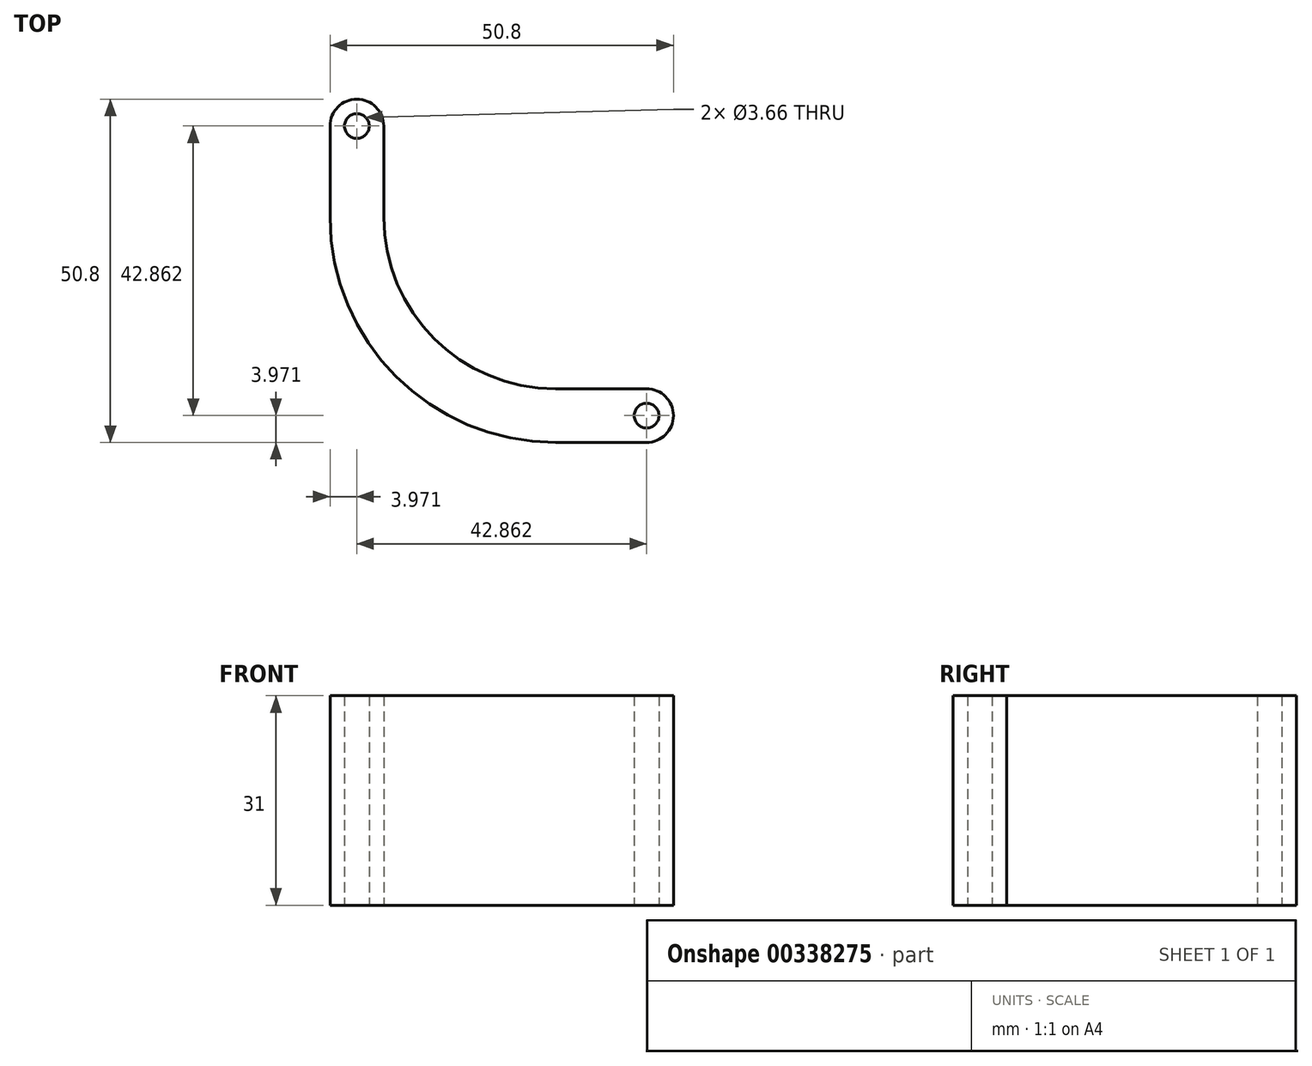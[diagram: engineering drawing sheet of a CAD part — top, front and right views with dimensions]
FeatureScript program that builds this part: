
annotation { "Feature Type Name" : "Feature", "Feature Type Description" : "" }
export const myFeature = defineFeature(function(context is Context, id is Id, definition is map)
    precondition{}
    {
        {
            var Q0;
            Q0=qCreatedBy(makeId("Top.planeOp"),FACE);
            var sketch = newSketch(context, id + "F0", { "sketchPlane" : qUnion([Q0])});
            skArc(sketch, "E0", {"start": v(-25.4, 0) * mm, "mid": v(-17.96, -17.96) * mm, "end": v(0, -25.4) * mm});
            skLineSegment(sketch, "E1.top", {"start": v(-25.4, 13.5) * mm, "end": v(-33.34, 13.5) * mm, "construction": true});
            skLineSegment(sketch, "E1.left", {"start": v(-25.4, 0) * mm, "end": v(-25.4, 13.5) * mm});
            skLineSegment(sketch, "E1.right", {"start": v(-33.34, 0) * mm, "end": v(-33.34, 13.5) * mm});
            skLineSegment(sketch, "E2.bottom", {"start": v(0, -25.4) * mm, "end": v(13.5, -25.4) * mm});
            skLineSegment(sketch, "E2.top", {"start": v(0, -33.34) * mm, "end": v(13.5, -33.34) * mm});
            skLineSegment(sketch, "E2.right", {"start": v(13.5, -25.4) * mm, "end": v(13.5, -33.34) * mm, "construction": true});
            skArc(sketch, "E3", {"start": v(-33.34, 0) * mm, "mid": v(-23.57, -23.57) * mm, "end": v(0, -33.34) * mm});
            skLineSegment(sketch, "E4", {"start": v(-33.34, 0) * mm, "end": v(-33.34, -33.34) * mm, "construction": true});
            skLineSegment(sketch, "E5", {"start": v(-33.34, -33.34) * mm, "end": v(0, -33.34) * mm, "construction": true});
            skArc(sketch, "E6", {"start": v(13.5, -33.34) * mm, "mid": v(17.46, -29.37) * mm, "end": v(13.5, -25.4) * mm});
            skArc(sketch, "E7", {"start": v(-25.4, 13.5) * mm, "mid": v(-29.37, 17.46) * mm, "end": v(-33.34, 13.5) * mm});
            skCircle(sketch, "E8", {"center": v(-29.37, 13.5) * mm, "radius": 1.83 * mm});
            skCircle(sketch, "E9", {"center": v(13.5, -29.37) * mm, "radius": 1.83 * mm});
            skLineSegment(sketch, "E10", {"start": v(0, -25.4) * mm, "end": v(0, -33.34) * mm, "construction": true});
            skLineSegment(sketch, "E11", {"start": v(17.46, -29.37) * mm, "end": v(0, -29.37) * mm, "construction": true});
            skSolve(sketch);
        }
        {
            var Q0;
            Q0 = qSketchRegion(id + "F0", true);
            extrude(context, id + "F1", {"entities" : qUnion([Q0]), "depth" : 31 * mm});
        }
    });
